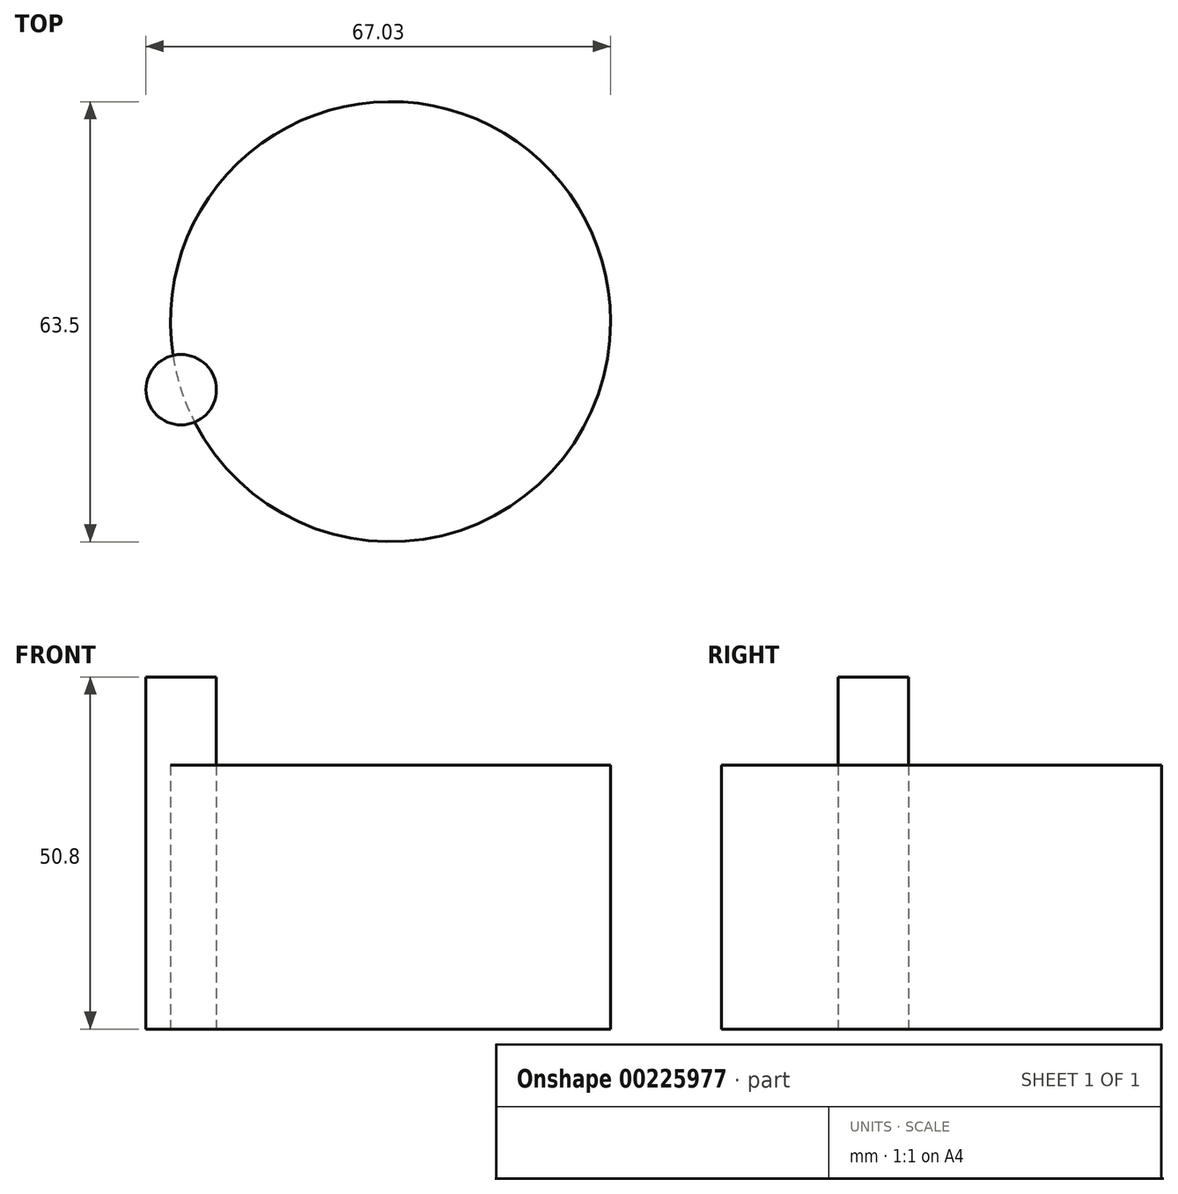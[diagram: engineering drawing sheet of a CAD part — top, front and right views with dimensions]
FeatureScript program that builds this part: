
annotation { "Feature Type Name" : "Feature", "Feature Type Description" : "" }
export const myFeature = defineFeature(function(context is Context, id is Id, definition is map)
    precondition{}
    {
        {
            var Q0;
            Q0=qCreatedBy(makeId("Top.planeOp"),FACE);
            var sketch = newSketch(context, id + "F0", { "sketchPlane" : qUnion([Q0])});
            skCircle(sketch, "E0", {"center": v(0, 0) * mm, "radius": 31.75 * mm});
            skSolve(sketch);
        }
        {
            var Q0;
            Q0=makeQuery(id+"F0.imprint","IMPRINT",FACE,{"disambiguationData":[TD([[makeQuery(id+"F0.imprint","IMPRINT",EDGE,{"derivedFrom":sQuery(id+"F0.wireOp",EDGE,"E0")}),1.0]])]});
            extrude(context, id + "F1", {"entities" : qUnion([Q0]), "depth" : 38.1 * mm});
        }
        {
            var Q0;
            Q0=qCreatedBy(makeId("Top.planeOp"),FACE);
            var sketch = newSketch(context, id + "F2", { "sketchPlane" : qUnion([Q0])});
            skCircle(sketch, "E1", {"center": v(0, 31.75) * mm, "radius": 5.08 * mm});
            skCircle(sketch, "E2.1.0", {"center": v(-18.66, 25.69) * mm, "radius": 5.08 * mm});
            skCircle(sketch, "E2.2.0", {"center": v(-30.2, 9.81) * mm, "radius": 5.08 * mm});
            skCircle(sketch, "E2.3.0", {"center": v(-30.2, -9.81) * mm, "radius": 5.08 * mm});
            skCircle(sketch, "E2.4.0", {"center": v(-18.66, -25.69) * mm, "radius": 5.08 * mm});
            skCircle(sketch, "E2.5.0", {"center": v(0, -31.75) * mm, "radius": 5.08 * mm});
            skCircle(sketch, "E2.6.0", {"center": v(18.66, -25.69) * mm, "radius": 5.08 * mm});
            skCircle(sketch, "E2.7.0", {"center": v(30.2, -9.81) * mm, "radius": 5.08 * mm});
            skCircle(sketch, "E2.8.0", {"center": v(30.2, 9.81) * mm, "radius": 5.08 * mm});
            skCircle(sketch, "E2.9.0", {"center": v(18.66, 25.69) * mm, "radius": 5.08 * mm});
            skPoint(sketch, "E2.center", {"position": v(0, 0) * mm});
            skSolve(sketch);
        }
        {
            var Q0;
            Q0=qSketchRegion(id+"F2",true);
            extrude(context, id + "F3", {"entities" : qUnion([Q0]), "depth" : 50.8 * mm});
        }
        {
            var Q0;
            Q0=makeQuery(id+"F3.opExtrude","SWEPT_BODY",BODY,{"disambiguationData":[OSD([sQuery(id+"F2.wireOp",EDGE,"E2.4.0")])]});
            var Q1;
            Q1=makeQuery(id+"F3.opExtrude","SWEPT_BODY",BODY,{"disambiguationData":[OSD([sQuery(id+"F2.wireOp",EDGE,"E2.5.0")])]});
            var Q2;
            Q2=makeQuery(id+"F3.opExtrude","SWEPT_BODY",BODY,{"disambiguationData":[OSD([sQuery(id+"F2.wireOp",EDGE,"E2.6.0")])]});
            var Q3;
            Q3=makeQuery(id+"F3.opExtrude","SWEPT_BODY",BODY,{"disambiguationData":[OSD([sQuery(id+"F2.wireOp",EDGE,"E2.7.0")])]});
            var Q4;
            Q4=makeQuery(id+"F3.opExtrude","SWEPT_BODY",BODY,{"disambiguationData":[OSD([sQuery(id+"F2.wireOp",EDGE,"E2.8.0")])]});
            var Q5;
            Q5=makeQuery(id+"F3.opExtrude","SWEPT_BODY",BODY,{"disambiguationData":[OSD([sQuery(id+"F2.wireOp",EDGE,"E2.9.0")])]});
            var Q6;
            Q6=makeQuery(id+"F3.opExtrude","SWEPT_BODY",BODY,{"disambiguationData":[OSD([sQuery(id+"F2.wireOp",EDGE,"E1")])]});
            var Q7;
            Q7=makeQuery(id+"F3.opExtrude","SWEPT_BODY",BODY,{"disambiguationData":[OSD([sQuery(id+"F2.wireOp",EDGE,"E2.1.0")])]});
            var Q8;
            Q8=makeQuery(id+"F3.opExtrude","SWEPT_BODY",BODY,{"disambiguationData":[OSD([sQuery(id+"F2.wireOp",EDGE,"E2.2.0")])]});
            var Q9;
            Q9=makeQuery(id+"F3.opExtrude","SWEPT_BODY",BODY,{"disambiguationData":[OSD([sQuery(id+"F2.wireOp",EDGE,"E2.3.0")])]});
            booleanBodies(context, id + "F4", {"operationType" : BooleanOperationType.INTERSECTION, "tools" : qUnion([Q0, Q1, Q2, Q3, Q4, Q5, Q6, Q7, Q8]), "targets" : qUnion([Q9])});
        }
    });
